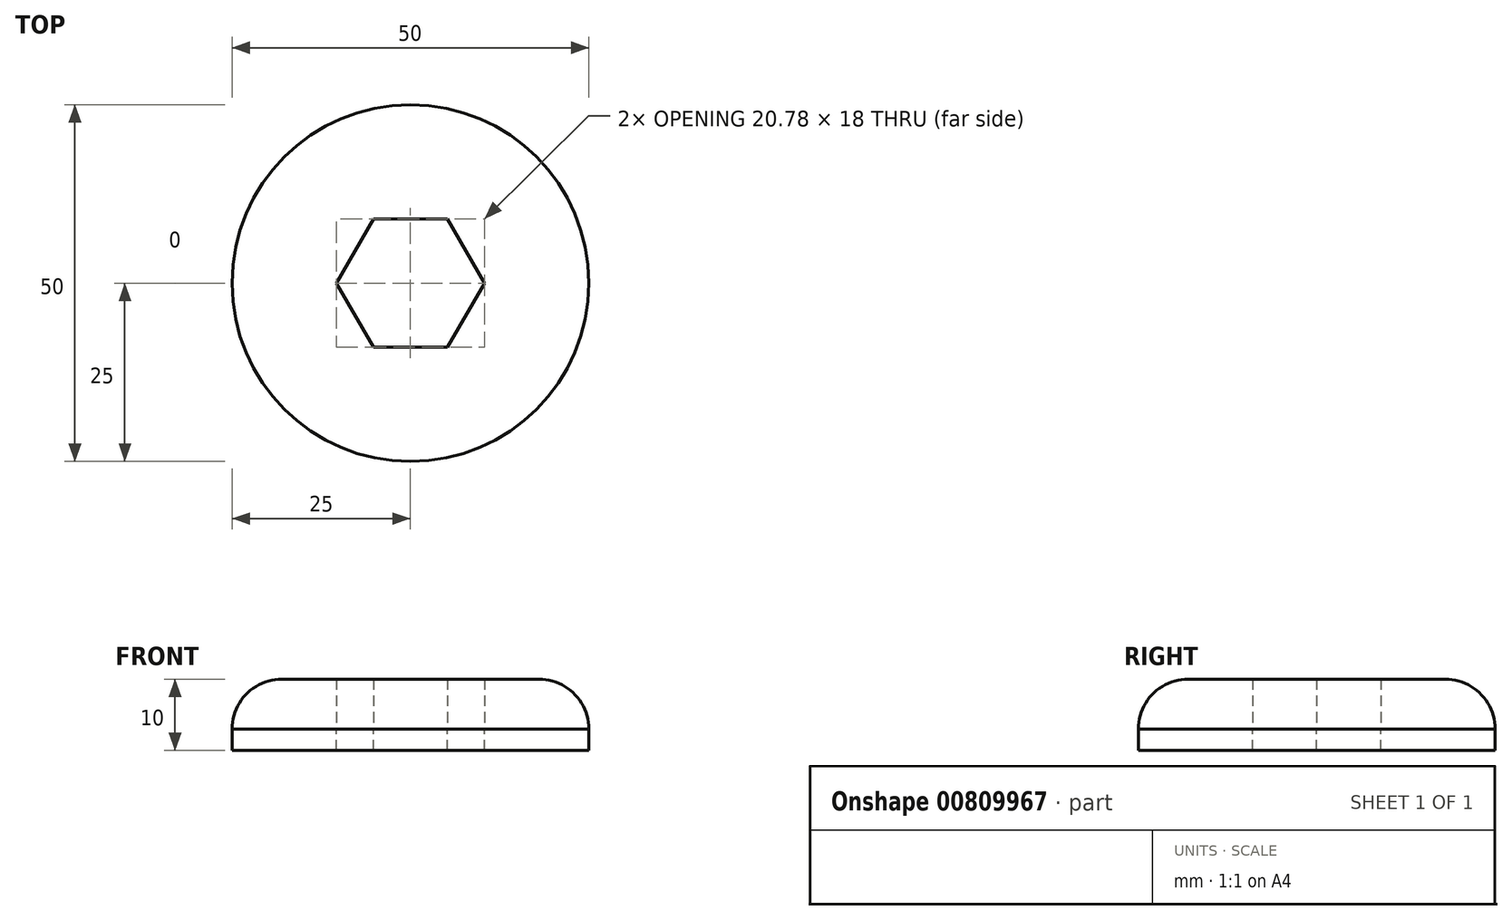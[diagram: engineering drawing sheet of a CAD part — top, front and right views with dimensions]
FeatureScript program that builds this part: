
annotation { "Feature Type Name" : "Feature", "Feature Type Description" : "" }
export const myFeature = defineFeature(function(context is Context, id is Id, definition is map)
    precondition{}
    {
        {
            var Q0;
            Q0=qCreatedBy(makeId("Top.planeOp"),FACE);
            var sketch = newSketch(context, id + "F0", { "sketchPlane" : qUnion([Q0])});
            skLineSegment(sketch, "E0", {"start": v(0, 0) * mm, "end": v(0, 9) * mm});
            skCircle(sketch, "E1.cCircle", {"center": v(0, 0) * mm, "radius": 9 * mm, "construction": true});
            skLineSegment(sketch, "E1.0", {"start": v(-5.2, 9) * mm, "end": v(5.2, 9) * mm});
            skLineSegment(sketch, "E1.1", {"start": v(5.2, 9) * mm, "end": v(10.4, 0) * mm});
            skLineSegment(sketch, "E1.2", {"start": v(10.4, 0) * mm, "end": v(5.2, -9) * mm});
            skLineSegment(sketch, "E1.3", {"start": v(5.2, -9) * mm, "end": v(-5.2, -9) * mm});
            skLineSegment(sketch, "E1.4", {"start": v(-5.2, -9) * mm, "end": v(-10.4, 0) * mm});
            skLineSegment(sketch, "E1.5", {"start": v(-10.4, 0) * mm, "end": v(-5.2, 9) * mm});
            skPoint(sketch, "E1.0.midPoint", {"position": v(0, 9) * mm});
            skCircle(sketch, "E2", {"center": v(0, 0) * mm, "radius": 25 * mm});
            skSolve(sketch);
        }
        {
            var Q0;
            {var subQ0=sQuery(id+"F0.wireOp",EDGE,"E1.1");Q0=makeQuery(id+"F0.imprint","IMPRINT",FACE,{"disambiguationData":[TD([[makeQuery(id+"F0.imprint","IMPRINT",EDGE,{"derivedFrom":subQ0}),1.0]])]});}
            extrude(context, id + "F1", {"entities" : qUnion([Q0]), "depth" : 7 * mm, "offsetDistance" : 25 * mm});
        }
        {
            var Q0;
            Q0=makeQuery(id+"F1.opExtrude","CAP_FACE",FACE,{"disambiguationData":[OSD([sQuery(id+"F0.wireOp",EDGE,"E1.0"),sQuery(id+"F0.wireOp",EDGE,"E1.1"),sQuery(id+"F0.wireOp",EDGE,"E1.2"),sQuery(id+"F0.wireOp",EDGE,"E1.3"),sQuery(id+"F0.wireOp",EDGE,"E1.4"),sQuery(id+"F0.wireOp",EDGE,"E1.5"),sQuery(id+"F0.wireOp",EDGE,"E2")])],"isStart":true});
            var sketch = newSketch(context, id + "F2", { "sketchPlane" : qUnion([Q0])});
            skCircle(sketch, "E3", {"center": v(0, 0) * mm, "radius": 25 * mm});
            skSolve(sketch);
        }
        {
            var Q0;
            Q0=makeQuery(id+"F2.imprint","IMPRINT",FACE,{"disambiguationData":[TD([[makeQuery(id+"F2.imprint","IMPRINT",EDGE,{"derivedFrom":makeQuery(id+"F1.opExtrude","CAP_EDGE",EDGE,{"disambiguationData":[OSD([sQuery(id+"F0.wireOp",EDGE,"E1.0")])],"isStart":true})}),1.0]])]});
            extrude(context, id + "F3", {"entities" : qUnion([Q0]), "depth" : 3 * mm, "offsetDistance" : 25 * mm});
        }
        {
            var Q0;
            Q0=makeQuery(id+"F1.opExtrude","CAP_FACE",FACE,{"disambiguationData":[OSD([sQuery(id+"F0.wireOp",EDGE,"E1.0"),sQuery(id+"F0.wireOp",EDGE,"E1.1"),sQuery(id+"F0.wireOp",EDGE,"E1.2"),sQuery(id+"F0.wireOp",EDGE,"E1.3"),sQuery(id+"F0.wireOp",EDGE,"E1.4"),sQuery(id+"F0.wireOp",EDGE,"E1.5"),sQuery(id+"F0.wireOp",EDGE,"E2")])],"isStart":true});
            extrude(context, id + "F4", {"entities" : qUnion([Q0]), "depth" : 3 * mm, "offsetDistance" : 25 * mm});
        }
        {
            var Q0;
            Q0=makeQuery(id+"F1.opExtrude","CAP_EDGE",EDGE,{"disambiguationData":[OSD([sQuery(id+"F0.wireOp",EDGE,"E2")])],"isStart":false});
            fillet(context, id + "F5", {"entities" : qUnion([Q0]), "radius" : 7 * mm, "tangentPropagation" : true, "allowEdgeOverflow" : false});
        }
    });
